# Revit family: Paper_Towel_Dispenser-Wall_Mounted-Bobrick-B-29744
name_source: partatom
category: Specialty Equipment
units: mm (PartAtom-declared; Revit-internal decimal feet)

## family parameters
Cut with Voids When Loaded = Yes
Host = Face
OmniClass Number = 23.40.20.21
OmniClass Title = Toilet and Bath Specialties
Part Type = Normal
Room Calculation Point = No
Round Connector Dimension = Use Diameter
Shared = No

## types (1)
- B-29744
    3974-57 AC External Adapter (6V) = No
    4 Alkaline “D” Cells (not included) = No
    ADA = Yes
    ADA Compliant = Yes
    Assembly Code = C1030200
    Cabinet Material = Stainless Steel-Bobrick-Satin
    Capacity = 8" Diameter 8" Wide Paper Towel Roll
    Default Elevation = 0"
    Description = Automatic, Universal Semi-Recessed Roll Towel Dispenser Equipped with LED Light
    Door Material = Stainless Steel-Bobrick-Satin
    Flange Material = Stainless Steel-Bobrick-Satin
    Height = 17 1/2"
    Installation Type = Recessed Wall Mounted
    Manufacturer = Bobrick Washroom Equipment, Inc.
    Material = Stainless Steel-Bobrick-Satin
    Minimum Recessed Depth = 4"
    Model = B-29744
    Mounting Height = 63 17/32"
    Mounting Height Constraint = 63 17/32"
    Product Page URL = https://www.bobrick.com
    Revised Date = 01/09/2023
    Shell Material = Stainless Steel-Bobrick-Satin
    Type Comments = 1-1/2" to 2" (38 to 51mm) diameter cores, up to 8" (205mm) diameter, 8" (205mm) wide, non-perforated, non-proprietary rolls. 800 ft (244 m) long.
    URL = https://www.bobrick.com
    Width = 14 5/8"

## geometry (parser evidence)
native form markers: Blend x4, Sweep x3
no freeform markers — native parametric forms only
